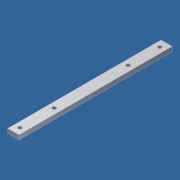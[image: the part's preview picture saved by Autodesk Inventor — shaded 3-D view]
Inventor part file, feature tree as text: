
AUTODESK INVENTOR PART (.ipt)
format: ipt  version: 2015 SP2 (Build 190223200, 223)  size: 97,792 bytes
history: native  units: mm (DEFAULTED — no unit token found)
features: other x8, sketch x1, extrude x1, hole x1
bodies: Solide1 (feature_tree)
feature tree (11):
  other  "Origine"
  sketch  "Esquisse7"
  extrude  "Extrusion3"  Depth=10.0mm
  hole  "Perçage3"  [1 undecoded]
  other  "Plan YZ"
  other  "Plan XZ"
  other  "Plan XY"
  other  "Axe X"
  other  "Axe Y"
  other  "Axe Z"
  other  "Point de centre"
note: 1 required parameter value undecoded (feature->parameter linkage not recoverable at this tier; creation-order binding heuristic only, values carry confidence <= 0.55)
